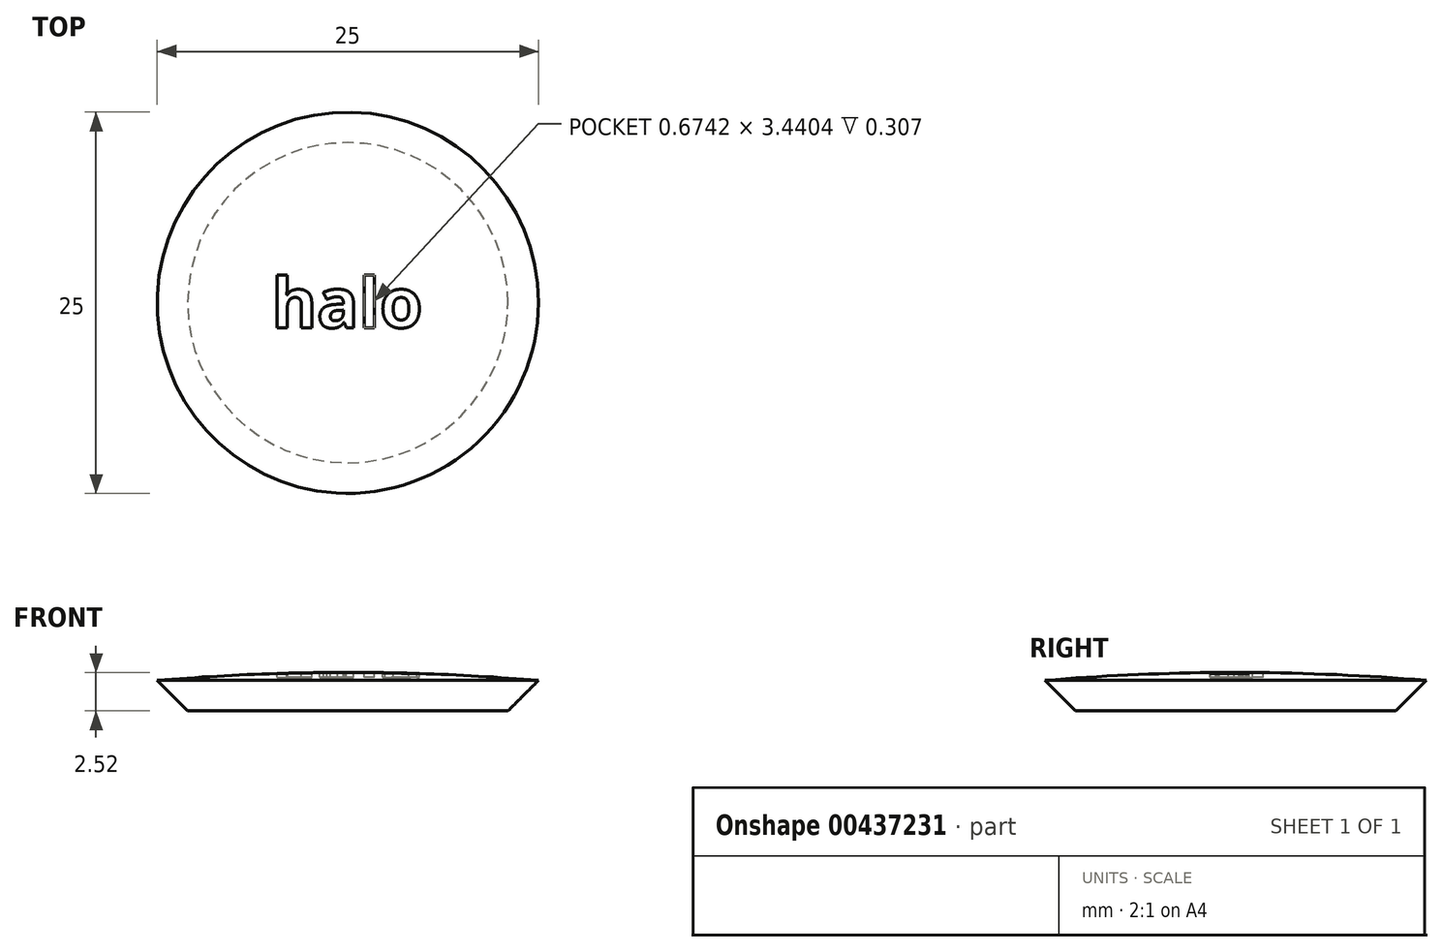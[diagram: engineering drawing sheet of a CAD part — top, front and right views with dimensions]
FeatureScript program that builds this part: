
annotation { "Feature Type Name" : "Feature", "Feature Type Description" : "" }
export const myFeature = defineFeature(function(context is Context, id is Id, definition is map)
    precondition{}
    {
        {
            var Q0;
            Q0=qCreatedBy(makeId("Right.planeOp"),FACE);
            var sketch = newSketch(context, id + "F0", { "sketchPlane" : qUnion([Q0])});
            skLineSegment(sketch, "E0", {"start": v(0, 0) * mm, "end": v(-10.5, 0) * mm});
            skLineSegment(sketch, "E1", {"start": v(-10.5, 0) * mm, "end": v(-12.5, 2) * mm});
            skArc(sketch, "E2", {"start": v(0, 2.52) * mm, "mid": v(-6.26, 2.4) * mm, "end": v(-12.5, 2) * mm});
            skLineSegment(sketch, "E3", {"start": v(0, 2.52) * mm, "end": v(0, 0) * mm});
            skLineSegment(sketch, "E4", {"start": v(0, 2.52) * mm, "end": v(4.5, 2.52) * mm, "construction": true});
            skSolve(sketch);
        }
        {
            var Q0;
            Q0=makeQuery(id+"F0.imprint","IMPRINT",FACE,{"disambiguationData":[TD([[makeQuery(id+"F0.imprint","IMPRINT",EDGE,{"derivedFrom":sQuery(id+"F0.wireOp",EDGE,"E0")}),-1.0]])]});
            var Q1;
            Q1=sQuery(id+"F0.wireOp",EDGE,"E3");
            revolve(context, id + "F1", {"entities" : qUnion([Q0]), "axis" : qUnion([Q1]), "revolveType" : RevolveType.FULL});
        }
        {
            var Q0;
            Q0=qCreatedBy(makeId("Top.planeOp"),FACE);
            cPlane(context, id + "F2", {"entities" : qUnion([Q0]), "cplaneType" : CPlaneType.OFFSET, "offset" : 30 * mm, "width" : 150 * mm, "height" : 150 * mm});
        }
        {
            var Q0;
            Q0=qCreatedBy(id+"F2.planeOp",FACE);
            var sketch = newSketch(context, id + "F3", { "sketchPlane" : qUnion([Q0])});
            skText(sketch, "E5", { "text": "halo", "fontName": "OpenSans-Bold.ttf"});
            const initialGuessF3  = {"E5": [-0.005, -0.00163, 1, 0, 0.00326]};
            skSetInitialGuess(sketch, initialGuessF3);
            skSolve(sketch);
        }
        {
            var Q0;
            Q0 = qSketchRegion(id + "F3", true);
            extrude(context, id + "F4", {"entities" : qUnion([Q0]), "operationType" : NewBodyOperationType.REMOVE, "oppositeDirection" : true, "depth" : 27.8 * mm});
        }
    });
